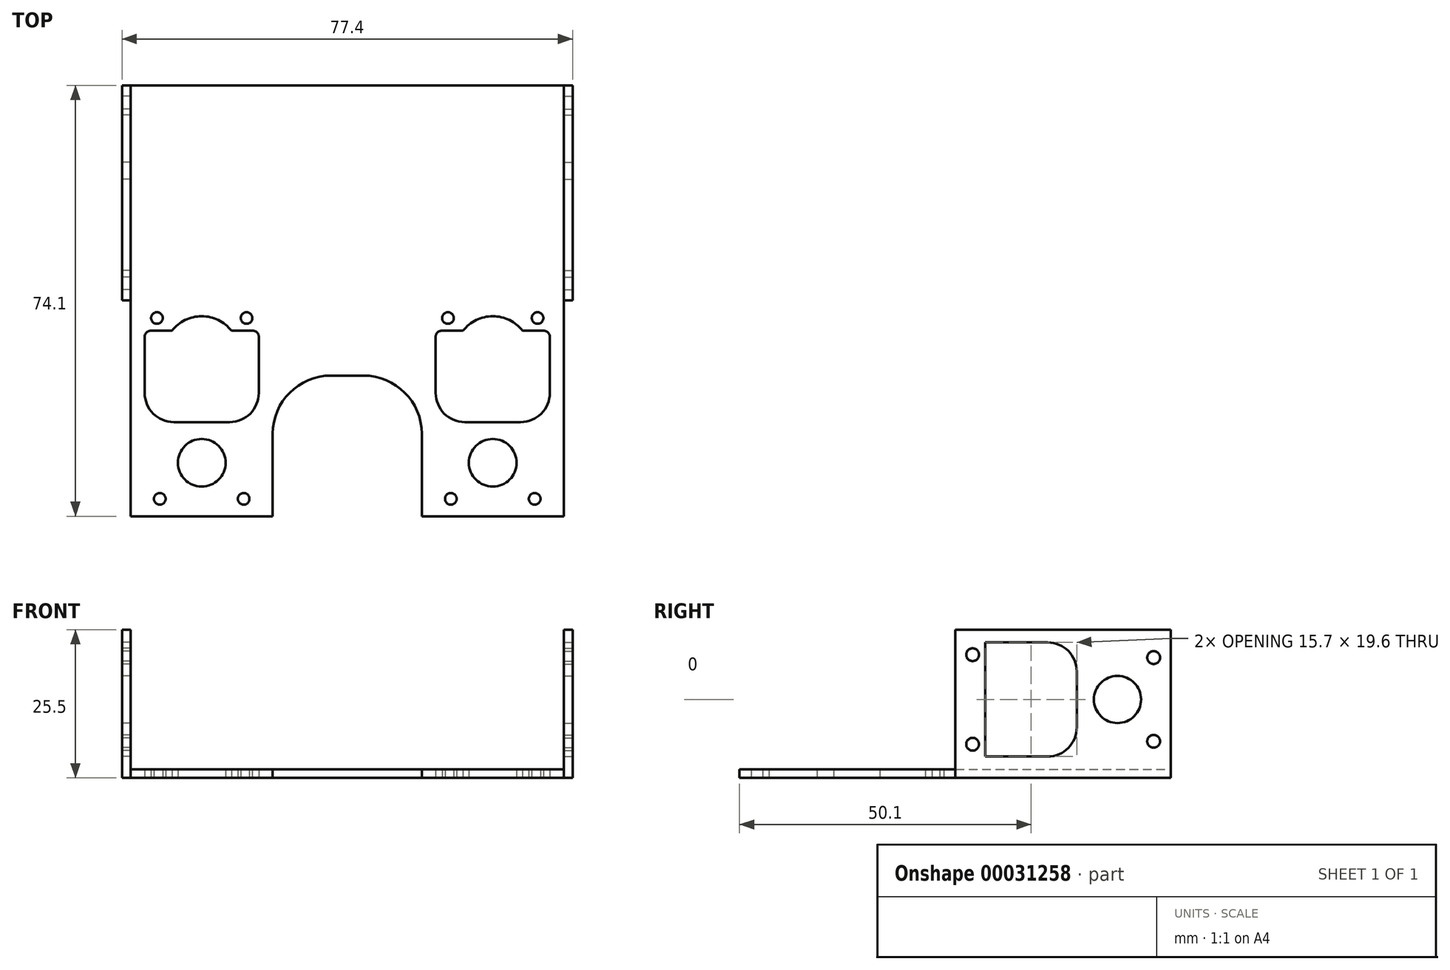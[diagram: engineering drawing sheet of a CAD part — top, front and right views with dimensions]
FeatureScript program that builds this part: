
annotation { "Feature Type Name" : "Feature", "Feature Type Description" : "" }
export const myFeature = defineFeature(function(context is Context, id is Id, definition is map)
    precondition{}
    {
        {
            var Q0;
            Q0=qCreatedBy(makeId("Top.planeOp"),FACE);
            var sketch = newSketch(context, id + "F0", { "sketchPlane" : qUnion([Q0])});
            skLineSegment(sketch, "E0.bottom", {"start": v(37.2, -19.55) * mm, "end": v(-37.2, -19.55) * mm});
            skLineSegment(sketch, "E0.top", {"start": v(37.2, 19.55) * mm, "end": v(-37.2, 19.55) * mm});
            skLineSegment(sketch, "E0.left", {"start": v(37.2, -19.55) * mm, "end": v(37.2, 19.55) * mm});
            skLineSegment(sketch, "E0.right", {"start": v(-37.2, -19.55) * mm, "end": v(-37.2, 19.55) * mm});
            skPoint(sketch, "E0.middle", {"position": v(0, 0) * mm});
            skCircle(sketch, "E1", {"center": v(25, 8.35) * mm, "radius": 4.1 * mm, "construction": true});
            skCircle(sketch, "E2", {"center": v(32.2, 14.55) * mm, "radius": 1 * mm, "construction": true});
            skLineSegment(sketch, "E3.bottom", {"start": v(33.8, -14.35) * mm, "end": v(30.12, -14.35) * mm, "construction": true});
            skLineSegment(sketch, "E3.top", {"start": v(29.8, 1.35) * mm, "end": v(20.2, 1.35) * mm, "construction": true});
            skLineSegment(sketch, "E3.left", {"start": v(34.8, -13.35) * mm, "end": v(34.8, -3.65) * mm, "construction": true});
            skLineSegment(sketch, "E3.right", {"start": v(15.2, -13.35) * mm, "end": v(15.2, -3.65) * mm, "construction": true});
            skPoint(sketch, "E3.middle", {"position": v(25, -6.5) * mm});
            skCircle(sketch, "E4", {"center": v(32.2, -16.55) * mm, "radius": 1 * mm});
            skPoint(sketch, "E5.visualSharp", {"position": v(15.2, 1.35) * mm});
            skArc(sketch, "E5.filletArc", {"start": v(20.2, 1.35) * mm, "mid": v(16.66, -0.11) * mm, "end": v(15.2, -3.65) * mm, "construction": true});
            skPoint(sketch, "E6.visualSharp", {"position": v(34.8, 1.35) * mm});
            skArc(sketch, "E6.filletArc", {"start": v(34.8, -3.65) * mm, "mid": v(33.34, -0.11) * mm, "end": v(29.8, 1.35) * mm, "construction": true});
            skPoint(sketch, "E7.visualSharp", {"position": v(15.2, -14.35) * mm});
            skArc(sketch, "E7.filletArc", {"start": v(15.2, -13.35) * mm, "mid": v(15.5, -14.06) * mm, "end": v(16.2, -14.35) * mm, "construction": true});
            skPoint(sketch, "E8.visualSharp", {"position": v(34.8, -14.35) * mm});
            skArc(sketch, "E8.filletArc", {"start": v(33.8, -14.35) * mm, "mid": v(34.5, -14.06) * mm, "end": v(34.8, -13.35) * mm, "construction": true});
            skArc(sketch, "E9", {"start": v(19.88, -14.35) * mm, "mid": v(25, -16.85) * mm, "end": v(30.12, -14.35) * mm, "construction": true});
            skLineSegment(sketch, "E10.trimOffspring", {"start": v(19.88, -14.35) * mm, "end": v(16.2, -14.35) * mm, "construction": true});
            skLineSegment(sketch, "E11", {"start": v(25, 19.55) * mm, "end": v(25, -19.55) * mm, "construction": true});
            skCircle(sketch, "E12.MirrorC", {"center": v(17.8, 14.55) * mm, "radius": 1 * mm, "construction": true});
            skCircle(sketch, "E13.MirrorC", {"center": v(17.8, -16.55) * mm, "radius": 1 * mm});
            skLineSegment(sketch, "E14", {"start": v(32.2, 14.55) * mm, "end": v(32.2, -16.55) * mm, "construction": true});
            skLineSegment(sketch, "E15", {"start": v(32.2, -1) * mm, "end": v(0, -1) * mm, "construction": true});
            skArc(sketch, "E16.MirrorCS", {"start": v(15.2, 11.35) * mm, "mid": v(15.5, 12.06) * mm, "end": v(16.2, 12.35) * mm});
            skArc(sketch, "E17.MirrorCS", {"start": v(33.8, 12.35) * mm, "mid": v(34.5, 12.06) * mm, "end": v(34.8, 11.35) * mm});
            skLineSegment(sketch, "E18.MirrorCS", {"start": v(15.2, 11.35) * mm, "end": v(15.2, 1.65) * mm});
            skLineSegment(sketch, "E19.MirrorCS", {"start": v(34.8, 11.35) * mm, "end": v(34.8, 1.65) * mm});
            skPoint(sketch, "E20.MirrorP", {"position": v(34.8, -3.35) * mm});
            skArc(sketch, "E21.MirrorCS", {"start": v(19.88, 12.35) * mm, "mid": v(25, 14.85) * mm, "end": v(30.12, 12.35) * mm});
            skPoint(sketch, "E22.MirrorP", {"position": v(15.2, -3.35) * mm});
            skPoint(sketch, "E23.MirrorP", {"position": v(25, 4.5) * mm});
            skCircle(sketch, "E24.MirrorC", {"center": v(25, -10.35) * mm, "radius": 4.1 * mm});
            skArc(sketch, "E25.MirrorCS", {"start": v(20.2, -3.35) * mm, "mid": v(16.66, -1.89) * mm, "end": v(15.2, 1.65) * mm});
            skLineSegment(sketch, "E26.MirrorCS", {"start": v(19.88, 12.35) * mm, "end": v(16.2, 12.35) * mm});
            skArc(sketch, "E27.MirrorCS", {"start": v(34.8, 1.65) * mm, "mid": v(33.34, -1.89) * mm, "end": v(29.8, -3.35) * mm});
            skPoint(sketch, "E28.MirrorP", {"position": v(34.8, 12.35) * mm});
            skLineSegment(sketch, "E29.MirrorCS", {"start": v(29.8, -3.35) * mm, "end": v(20.2, -3.35) * mm});
            skLineSegment(sketch, "E30.MirrorCS", {"start": v(33.8, 12.35) * mm, "end": v(30.12, 12.35) * mm});
            skPoint(sketch, "E31.MirrorP", {"position": v(15.2, 12.35) * mm});
            skArc(sketch, "E32.MirrorCS", {"start": v(-15.2, -13.35) * mm, "mid": v(-15.5, -14.06) * mm, "end": v(-16.2, -14.35) * mm, "construction": true});
            skArc(sketch, "E33.MirrorCS", {"start": v(-33.8, -14.35) * mm, "mid": v(-34.5, -14.06) * mm, "end": v(-34.8, -13.35) * mm, "construction": true});
            skArc(sketch, "E34.MirrorCS", {"start": v(-33.8, 12.35) * mm, "mid": v(-34.5, 12.06) * mm, "end": v(-34.8, 11.35) * mm});
            skArc(sketch, "E35.MirrorCS", {"start": v(-15.2, 11.35) * mm, "mid": v(-15.5, 12.06) * mm, "end": v(-16.2, 12.35) * mm});
            skPoint(sketch, "E36.MirrorP", {"position": v(-34.8, -14.35) * mm});
            skCircle(sketch, "E37.MirrorC", {"center": v(-25, 8.35) * mm, "radius": 4.1 * mm, "construction": true});
            skLineSegment(sketch, "E38.MirrorCS", {"start": v(-15.2, 11.35) * mm, "end": v(-15.2, 1.65) * mm});
            skArc(sketch, "E39.MirrorCS", {"start": v(-19.88, -14.35) * mm, "mid": v(-25, -16.85) * mm, "end": v(-30.12, -14.35) * mm, "construction": true});
            skCircle(sketch, "E40.MirrorC", {"center": v(-32.2, -16.55) * mm, "radius": 1 * mm});
            skLineSegment(sketch, "E41.MirrorCS", {"start": v(-33.8, -14.35) * mm, "end": v(-30.12, -14.35) * mm, "construction": true});
            skLineSegment(sketch, "E42.MirrorCS", {"start": v(-34.8, -13.35) * mm, "end": v(-34.8, -3.65) * mm, "construction": true});
            skCircle(sketch, "E43.MirrorC", {"center": v(-17.8, -16.55) * mm, "radius": 1 * mm});
            skPoint(sketch, "E44.MirrorP", {"position": v(-25, -6.5) * mm});
            skLineSegment(sketch, "E45.MirrorCS", {"start": v(-15.2, -13.35) * mm, "end": v(-15.2, -3.65) * mm, "construction": true});
            skPoint(sketch, "E46.MirrorP", {"position": v(-34.8, 12.35) * mm});
            skLineSegment(sketch, "E47.MirrorCS", {"start": v(-32.2, 14.55) * mm, "end": v(-32.2, -16.55) * mm, "construction": true});
            skLineSegment(sketch, "E48.MirrorCS", {"start": v(-34.8, 11.35) * mm, "end": v(-34.8, 1.65) * mm});
            skLineSegment(sketch, "E49.MirrorCS", {"start": v(-33.8, 12.35) * mm, "end": v(-30.12, 12.35) * mm});
            skArc(sketch, "E50.MirrorCS", {"start": v(-20.2, -3.35) * mm, "mid": v(-16.66, -1.89) * mm, "end": v(-15.2, 1.65) * mm});
            skArc(sketch, "E51.MirrorCS", {"start": v(-19.88, 12.35) * mm, "mid": v(-25, 14.85) * mm, "end": v(-30.12, 12.35) * mm});
            skLineSegment(sketch, "E52.MirrorCS", {"start": v(-19.88, 12.35) * mm, "end": v(-16.2, 12.35) * mm});
            skArc(sketch, "E53.MirrorCS", {"start": v(-34.8, -3.65) * mm, "mid": v(-33.34, -0.11) * mm, "end": v(-29.8, 1.35) * mm, "construction": true});
            skPoint(sketch, "E54.MirrorP", {"position": v(-15.2, 1.35) * mm});
            skCircle(sketch, "E55.MirrorC", {"center": v(-32.2, 14.55) * mm, "radius": 1 * mm, "construction": true});
            skPoint(sketch, "E56.MirrorP", {"position": v(-34.8, 1.35) * mm});
            skPoint(sketch, "E57.MirrorP", {"position": v(-15.2, -3.35) * mm});
            skLineSegment(sketch, "E58.MirrorCS", {"start": v(-29.8, 1.35) * mm, "end": v(-20.2, 1.35) * mm, "construction": true});
            skLineSegment(sketch, "E59.MirrorCS", {"start": v(-29.8, -3.35) * mm, "end": v(-20.2, -3.35) * mm});
            skPoint(sketch, "E60.MirrorP", {"position": v(-34.8, -3.35) * mm});
            skArc(sketch, "E61.MirrorCS", {"start": v(-20.2, 1.35) * mm, "mid": v(-16.66, -0.11) * mm, "end": v(-15.2, -3.65) * mm, "construction": true});
            skCircle(sketch, "E62.MirrorC", {"center": v(-25, -10.35) * mm, "radius": 4.1 * mm});
            skPoint(sketch, "E63.MirrorP", {"position": v(-15.2, -14.35) * mm});
            skPoint(sketch, "E64.MirrorP", {"position": v(-15.2, 12.35) * mm});
            skPoint(sketch, "E65.MirrorP", {"position": v(-25, 4.5) * mm});
            skArc(sketch, "E66.MirrorCS", {"start": v(-34.8, 1.65) * mm, "mid": v(-33.34, -1.89) * mm, "end": v(-29.8, -3.35) * mm});
            skCircle(sketch, "E67.MirrorC", {"center": v(-17.8, 14.55) * mm, "radius": 1 * mm, "construction": true});
            skLineSegment(sketch, "E68.MirrorCS", {"start": v(-19.88, -14.35) * mm, "end": v(-16.2, -14.35) * mm, "construction": true});
            skCircle(sketch, "E69", {"center": v(32.7, 14.55) * mm, "radius": 1 * mm, "construction": true});
            skCircle(sketch, "E70.MirrorC", {"center": v(17.3, 14.55) * mm, "radius": 1 * mm, "construction": true});
            skCircle(sketch, "E71.MirrorC", {"center": v(-32.7, 14.55) * mm, "radius": 1 * mm});
            skCircle(sketch, "E72.MirrorC", {"center": v(-17.3, 14.55) * mm, "radius": 1 * mm});
            skCircle(sketch, "E73", {"center": v(32.7, 14.55) * mm, "radius": 1 * mm});
            skCircle(sketch, "E74.MirrorC", {"center": v(17.3, 14.55) * mm, "radius": 1 * mm});
            skSolve(sketch);
        }
        {
            var Q0;
            Q0=qSketchRegion(id+"F0",true);
            extrude(context, id + "F1", {"entities" : qUnion([Q0]), "depth" : 1.5 * mm});
        }
        {
            var Q0;
            Q0=makeQuery(id+"F1.opExtrude","CAP_FACE",FACE,{"disambiguationData":[OSD([sQuery(id+"F0.wireOp",EDGE,"E0.bottom"),sQuery(id+"F0.wireOp",EDGE,"E0.top"),sQuery(id+"F0.wireOp",EDGE,"E0.left"),sQuery(id+"F0.wireOp",EDGE,"E0.right"),sQuery(id+"F0.wireOp",EDGE,"E2"),sQuery(id+"F0.wireOp",EDGE,"E4"),sQuery(id+"F0.wireOp",EDGE,"E12.MirrorC"),sQuery(id+"F0.wireOp",EDGE,"E13.MirrorC"),sQuery(id+"F0.wireOp",EDGE,"E16.MirrorCS"),sQuery(id+"F0.wireOp",EDGE,"E17.MirrorCS"),sQuery(id+"F0.wireOp",EDGE,"E18.MirrorCS"),sQuery(id+"F0.wireOp",EDGE,"E19.MirrorCS"),sQuery(id+"F0.wireOp",EDGE,"E21.MirrorCS"),sQuery(id+"F0.wireOp",EDGE,"E24.MirrorC"),sQuery(id+"F0.wireOp",EDGE,"E25.MirrorCS"),sQuery(id+"F0.wireOp",EDGE,"E26.MirrorCS"),sQuery(id+"F0.wireOp",EDGE,"E27.MirrorCS"),sQuery(id+"F0.wireOp",EDGE,"E29.MirrorCS"),sQuery(id+"F0.wireOp",EDGE,"E30.MirrorCS"),sQuery(id+"F0.wireOp",EDGE,"E34.MirrorCS"),sQuery(id+"F0.wireOp",EDGE,"E35.MirrorCS"),sQuery(id+"F0.wireOp",EDGE,"E38.MirrorCS"),sQuery(id+"F0.wireOp",EDGE,"E40.MirrorC"),sQuery(id+"F0.wireOp",EDGE,"E43.MirrorC"),sQuery(id+"F0.wireOp",EDGE,"E48.MirrorCS"),sQuery(id+"F0.wireOp",EDGE,"E49.MirrorCS"),sQuery(id+"F0.wireOp",EDGE,"E50.MirrorCS"),sQuery(id+"F0.wireOp",EDGE,"E51.MirrorCS"),sQuery(id+"F0.wireOp",EDGE,"E52.MirrorCS"),sQuery(id+"F0.wireOp",EDGE,"E55.MirrorC"),sQuery(id+"F0.wireOp",EDGE,"E59.MirrorCS"),sQuery(id+"F0.wireOp",EDGE,"E62.MirrorC"),sQuery(id+"F0.wireOp",EDGE,"E66.MirrorCS"),sQuery(id+"F0.wireOp",EDGE,"E67.MirrorC")])],"isStart":false});
            var sketch = newSketch(context, id + "F2", { "sketchPlane" : qUnion([Q0])});
            skLineSegment(sketch, "E75.bottom", {"start": v(-37.2, 19.55) * mm, "end": v(37.2, 19.55) * mm});
            skLineSegment(sketch, "E75.top", {"start": v(-37.2, 54.55) * mm, "end": v(37.2, 54.55) * mm});
            skLineSegment(sketch, "E75.left", {"start": v(-37.2, 19.55) * mm, "end": v(-37.2, 54.55) * mm});
            skLineSegment(sketch, "E75.right", {"start": v(37.2, 19.55) * mm, "end": v(37.2, 54.55) * mm});
            skPoint(sketch, "E76", {"position": v(-25, -10.35) * mm});
            skSolve(sketch);
        }
        {
            var Q0;
            Q0 = qSketchRegion(id + "F2", true);
            extrude(context, id + "F3", {"entities" : qUnion([Q0]), "operationType" : NewBodyOperationType.ADD, "oppositeDirection" : true, "depth" : 1.5 * mm});
        }
        {
            var Q0;
            Q0=makeQuery(id+"F3.boolean.opBoolean","MERGE",FACE,{"derivedFrom":[makeQuery(id+"F1.opExtrude","CAP_FACE",FACE,{"disambiguationData":[OSD([sQuery(id+"F0.wireOp",EDGE,"E0.bottom"),sQuery(id+"F0.wireOp",EDGE,"E0.top"),sQuery(id+"F0.wireOp",EDGE,"E0.left"),sQuery(id+"F0.wireOp",EDGE,"E0.right"),sQuery(id+"F0.wireOp",EDGE,"E2"),sQuery(id+"F0.wireOp",EDGE,"E4"),sQuery(id+"F0.wireOp",EDGE,"E12.MirrorC"),sQuery(id+"F0.wireOp",EDGE,"E13.MirrorC"),sQuery(id+"F0.wireOp",EDGE,"E16.MirrorCS"),sQuery(id+"F0.wireOp",EDGE,"E17.MirrorCS"),sQuery(id+"F0.wireOp",EDGE,"E18.MirrorCS"),sQuery(id+"F0.wireOp",EDGE,"E19.MirrorCS"),sQuery(id+"F0.wireOp",EDGE,"E21.MirrorCS"),sQuery(id+"F0.wireOp",EDGE,"E24.MirrorC"),sQuery(id+"F0.wireOp",EDGE,"E25.MirrorCS"),sQuery(id+"F0.wireOp",EDGE,"E26.MirrorCS"),sQuery(id+"F0.wireOp",EDGE,"E27.MirrorCS"),sQuery(id+"F0.wireOp",EDGE,"E29.MirrorCS"),sQuery(id+"F0.wireOp",EDGE,"E30.MirrorCS"),sQuery(id+"F0.wireOp",EDGE,"E34.MirrorCS"),sQuery(id+"F0.wireOp",EDGE,"E35.MirrorCS"),sQuery(id+"F0.wireOp",EDGE,"E38.MirrorCS"),sQuery(id+"F0.wireOp",EDGE,"E40.MirrorC"),sQuery(id+"F0.wireOp",EDGE,"E43.MirrorC"),sQuery(id+"F0.wireOp",EDGE,"E48.MirrorCS"),sQuery(id+"F0.wireOp",EDGE,"E49.MirrorCS"),sQuery(id+"F0.wireOp",EDGE,"E50.MirrorCS"),sQuery(id+"F0.wireOp",EDGE,"E51.MirrorCS"),sQuery(id+"F0.wireOp",EDGE,"E52.MirrorCS"),sQuery(id+"F0.wireOp",EDGE,"E55.MirrorC"),sQuery(id+"F0.wireOp",EDGE,"E59.MirrorCS"),sQuery(id+"F0.wireOp",EDGE,"E62.MirrorC"),sQuery(id+"F0.wireOp",EDGE,"E66.MirrorCS"),sQuery(id+"F0.wireOp",EDGE,"E67.MirrorC")])],"isStart":false}),makeQuery(id+"F3.opExtrude","CAP_FACE",FACE,{"disambiguationData":[OSD([sQuery(id+"F2.wireOp",EDGE,"E75.bottom"),sQuery(id+"F2.wireOp",EDGE,"E75.top"),sQuery(id+"F2.wireOp",EDGE,"E75.left"),sQuery(id+"F2.wireOp",EDGE,"E75.right")])],"isStart":true})]});
            var sketch = newSketch(context, id + "F4", { "sketchPlane" : qUnion([Q0])});
            skLineSegment(sketch, "E77.bottom", {"start": v(-12.8, -19.55) * mm, "end": v(12.8, -19.55) * mm});
            skLineSegment(sketch, "E77.top", {"start": v(-12.8, 4.65) * mm, "end": v(12.8, 4.65) * mm});
            skLineSegment(sketch, "E77.left", {"start": v(-12.8, -19.55) * mm, "end": v(-12.8, 4.65) * mm});
            skLineSegment(sketch, "E77.right", {"start": v(12.8, -19.55) * mm, "end": v(12.8, 4.65) * mm});
            skPoint(sketch, "E78", {"position": v(0, -19.55) * mm});
            skPoint(sketch, "E79", {"position": v(-25, -10.35) * mm});
            skPoint(sketch, "E80", {"position": v(-32.2, -16.55) * mm});
            skPoint(sketch, "E81", {"position": v(-17.8, -16.55) * mm});
            skSolve(sketch);
        }
        {
            var Q0;
            Q0 = qSketchRegion(id + "F4", true);
            extrude(context, id + "F5", {"entities" : qUnion([Q0]), "operationType" : NewBodyOperationType.REMOVE, "endBound" : BoundingType.UP_TO_NEXT, "oppositeDirection" : true, "depth" : 25 * mm});
        }
        {
            var Q0;
            Q0=makeQuery(id+"F5.boolean.opBoolean","COPY",EDGE,{"derivedFrom":makeQuery(id+"F5.opExtrude","SWEPT_EDGE",EDGE,{"disambiguationData":[OSD([sQuery(id+"F4.wireOp",EDGE,"E77.top"),sQuery(id+"F4.wireOp",EDGE,"E77.left")])]})});
            var Q1;
            Q1=makeQuery(id+"F5.boolean.opBoolean","COPY",EDGE,{"derivedFrom":makeQuery(id+"F5.opExtrude","SWEPT_EDGE",EDGE,{"disambiguationData":[OSD([sQuery(id+"F4.wireOp",EDGE,"E77.top"),sQuery(id+"F4.wireOp",EDGE,"E77.right")])]})});
            fillet(context, id + "F6", {"entities" : qUnion([Q0, Q1]), "radius" : 10 * mm, "tangentPropagation" : true, "allowEdgeOverflow" : false});
        }
        {
            var Q0;
            Q0=makeQuery(id+"F3.boolean.opBoolean","MERGE",FACE,{"derivedFrom":[makeQuery(id+"F1.opExtrude","CAP_FACE",FACE,{"disambiguationData":[OSD([sQuery(id+"F0.wireOp",EDGE,"E0.bottom"),sQuery(id+"F0.wireOp",EDGE,"E0.top"),sQuery(id+"F0.wireOp",EDGE,"E0.left"),sQuery(id+"F0.wireOp",EDGE,"E0.right"),sQuery(id+"F0.wireOp",EDGE,"E2"),sQuery(id+"F0.wireOp",EDGE,"E4"),sQuery(id+"F0.wireOp",EDGE,"E12.MirrorC"),sQuery(id+"F0.wireOp",EDGE,"E13.MirrorC"),sQuery(id+"F0.wireOp",EDGE,"E16.MirrorCS"),sQuery(id+"F0.wireOp",EDGE,"E17.MirrorCS"),sQuery(id+"F0.wireOp",EDGE,"E18.MirrorCS"),sQuery(id+"F0.wireOp",EDGE,"E19.MirrorCS"),sQuery(id+"F0.wireOp",EDGE,"E21.MirrorCS"),sQuery(id+"F0.wireOp",EDGE,"E24.MirrorC"),sQuery(id+"F0.wireOp",EDGE,"E25.MirrorCS"),sQuery(id+"F0.wireOp",EDGE,"E26.MirrorCS"),sQuery(id+"F0.wireOp",EDGE,"E27.MirrorCS"),sQuery(id+"F0.wireOp",EDGE,"E29.MirrorCS"),sQuery(id+"F0.wireOp",EDGE,"E30.MirrorCS"),sQuery(id+"F0.wireOp",EDGE,"E34.MirrorCS"),sQuery(id+"F0.wireOp",EDGE,"E35.MirrorCS"),sQuery(id+"F0.wireOp",EDGE,"E38.MirrorCS"),sQuery(id+"F0.wireOp",EDGE,"E40.MirrorC"),sQuery(id+"F0.wireOp",EDGE,"E43.MirrorC"),sQuery(id+"F0.wireOp",EDGE,"E48.MirrorCS"),sQuery(id+"F0.wireOp",EDGE,"E49.MirrorCS"),sQuery(id+"F0.wireOp",EDGE,"E50.MirrorCS"),sQuery(id+"F0.wireOp",EDGE,"E51.MirrorCS"),sQuery(id+"F0.wireOp",EDGE,"E52.MirrorCS"),sQuery(id+"F0.wireOp",EDGE,"E55.MirrorC"),sQuery(id+"F0.wireOp",EDGE,"E59.MirrorCS"),sQuery(id+"F0.wireOp",EDGE,"E62.MirrorC"),sQuery(id+"F0.wireOp",EDGE,"E66.MirrorCS"),sQuery(id+"F0.wireOp",EDGE,"E67.MirrorC")])],"isStart":false}),makeQuery(id+"F3.opExtrude","CAP_FACE",FACE,{"disambiguationData":[OSD([sQuery(id+"F2.wireOp",EDGE,"E75.bottom"),sQuery(id+"F2.wireOp",EDGE,"E75.top"),sQuery(id+"F2.wireOp",EDGE,"E75.left"),sQuery(id+"F2.wireOp",EDGE,"E75.right")])],"isStart":true})]});
            var sketch = newSketch(context, id + "F7", { "sketchPlane" : qUnion([Q0])});
            skLineSegment(sketch, "E82.bottom", {"start": v(37.2, 54.55) * mm, "end": v(38.7, 54.55) * mm});
            skLineSegment(sketch, "E82.top", {"start": v(37.2, 17.55) * mm, "end": v(38.7, 17.55) * mm});
            skLineSegment(sketch, "E82.left", {"start": v(37.2, 54.55) * mm, "end": v(37.2, 17.55) * mm});
            skLineSegment(sketch, "E82.right", {"start": v(38.7, 54.55) * mm, "end": v(38.7, 17.55) * mm});
            skSolve(sketch);
        }
        {
            var Q0;
            Q0 = qSketchRegion(id + "F7", true);
            extrude(context, id + "F8", {"entities" : qUnion([Q0]), "operationType" : NewBodyOperationType.ADD, "depth" : (20 + 4) * mm, "hasSecondDirection" : true, "secondDirectionOppositeDirection" : true, "secondDirectionDepth" : 1.5 * mm});
        }
        {
            var Q0;
            Q0=makeQuery(id+"F8.opExtrude","SWEPT_FACE",FACE,{"disambiguationData":[OSD([sQuery(id+"F7.wireOp",EDGE,"E82.right")])]});
            var sketch = newSketch(context, id + "F9", { "sketchPlane" : qUnion([Q0])});
            skLineSegment(sketch, "E83", {"start": v(54.55, 13.5) * mm, "end": v(17.55, 13.5) * mm, "construction": true});
            skLineSegment(sketch, "E84", {"start": v(36.05, 25.5) * mm, "end": v(36.05, 0) * mm, "construction": true});
            skCircle(sketch, "E85", {"center": v(51.6, 20.7) * mm, "radius": 1.1 * mm});
            skCircle(sketch, "E86", {"center": v(45.4, 13.5) * mm, "radius": 4.05 * mm});
            skLineSegment(sketch, "E87.bottom", {"start": v(33.4, 23.3) * mm, "end": v(22.7, 23.3) * mm});
            skLineSegment(sketch, "E87.top", {"start": v(33.4, 3.7) * mm, "end": v(22.7, 3.7) * mm});
            skLineSegment(sketch, "E87.left", {"start": v(38.4, 18.3) * mm, "end": v(38.4, 8.7) * mm});
            skLineSegment(sketch, "E87.right", {"start": v(22.7, 23.3) * mm, "end": v(22.7, 3.7) * mm});
            skPoint(sketch, "E87.middle", {"position": v(30.55, 13.5) * mm});
            skPoint(sketch, "E88.visualSharp", {"position": v(38.4, 23.3) * mm});
            skArc(sketch, "E88.filletArc", {"start": v(38.4, 18.3) * mm, "mid": v(36.94, 21.84) * mm, "end": v(33.4, 23.3) * mm});
            skPoint(sketch, "E89.visualSharp", {"position": v(38.4, 3.7) * mm});
            skArc(sketch, "E89.filletArc", {"start": v(33.4, 3.7) * mm, "mid": v(36.94, 5.16) * mm, "end": v(38.4, 8.7) * mm});
            skCircle(sketch, "E90.MirrorC", {"center": v(51.6, 6.3) * mm, "radius": 1.1 * mm});
            skCircle(sketch, "E91.MirrorC", {"center": v(20.5, 20.7) * mm, "radius": 1.1 * mm, "construction": true});
            skCircle(sketch, "E92.MirrorC", {"center": v(20.5, 6.3) * mm, "radius": 1.1 * mm, "construction": true});
            skCircle(sketch, "E93", {"center": v(20.5, 21.2) * mm, "radius": 1.1 * mm});
            skCircle(sketch, "E94.MirrorC", {"center": v(20.5, 5.8) * mm, "radius": 1.1 * mm});
            skSolve(sketch);
        }
        {
            var Q0;
            Q0 = qSketchRegion(id + "F9", true);
            extrude(context, id + "F10", {"entities" : qUnion([Q0]), "operationType" : NewBodyOperationType.REMOVE, "endBound" : BoundingType.UP_TO_NEXT, "oppositeDirection" : true, "depth" : 25 * mm});
        }
        {
            var Q0;
            Q0=makeQuery(id+"F1.opExtrude","SWEPT_BODY",BODY,{"disambiguationData":[OSD([sQuery(id+"F0.wireOp",EDGE,"E0.bottom"),sQuery(id+"F0.wireOp",EDGE,"E0.top"),sQuery(id+"F0.wireOp",EDGE,"E0.left"),sQuery(id+"F0.wireOp",EDGE,"E0.right"),sQuery(id+"F0.wireOp",EDGE,"E2"),sQuery(id+"F0.wireOp",EDGE,"E4"),sQuery(id+"F0.wireOp",EDGE,"E12.MirrorC"),sQuery(id+"F0.wireOp",EDGE,"E13.MirrorC"),sQuery(id+"F0.wireOp",EDGE,"E16.MirrorCS"),sQuery(id+"F0.wireOp",EDGE,"E17.MirrorCS"),sQuery(id+"F0.wireOp",EDGE,"E18.MirrorCS"),sQuery(id+"F0.wireOp",EDGE,"E19.MirrorCS"),sQuery(id+"F0.wireOp",EDGE,"E21.MirrorCS"),sQuery(id+"F0.wireOp",EDGE,"E24.MirrorC"),sQuery(id+"F0.wireOp",EDGE,"E25.MirrorCS"),sQuery(id+"F0.wireOp",EDGE,"E26.MirrorCS"),sQuery(id+"F0.wireOp",EDGE,"E27.MirrorCS"),sQuery(id+"F0.wireOp",EDGE,"E29.MirrorCS"),sQuery(id+"F0.wireOp",EDGE,"E30.MirrorCS"),sQuery(id+"F0.wireOp",EDGE,"E34.MirrorCS"),sQuery(id+"F0.wireOp",EDGE,"E35.MirrorCS"),sQuery(id+"F0.wireOp",EDGE,"E38.MirrorCS"),sQuery(id+"F0.wireOp",EDGE,"E40.MirrorC"),sQuery(id+"F0.wireOp",EDGE,"E43.MirrorC"),sQuery(id+"F0.wireOp",EDGE,"E48.MirrorCS"),sQuery(id+"F0.wireOp",EDGE,"E49.MirrorCS"),sQuery(id+"F0.wireOp",EDGE,"E50.MirrorCS"),sQuery(id+"F0.wireOp",EDGE,"E51.MirrorCS"),sQuery(id+"F0.wireOp",EDGE,"E52.MirrorCS"),sQuery(id+"F0.wireOp",EDGE,"E55.MirrorC"),sQuery(id+"F0.wireOp",EDGE,"E59.MirrorCS"),sQuery(id+"F0.wireOp",EDGE,"E62.MirrorC"),sQuery(id+"F0.wireOp",EDGE,"E66.MirrorCS"),sQuery(id+"F0.wireOp",EDGE,"E67.MirrorC")])]});
            var Q1;
            Q1=qCreatedBy(makeId("Right.planeOp"),FACE);
            mirror(context, id + "F11", {"operationType" : NewBodyOperationType.ADD, "entities" : qUnion([Q0]), "mirrorPlane" : qUnion([Q1])});
        }
    });
